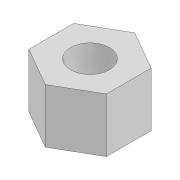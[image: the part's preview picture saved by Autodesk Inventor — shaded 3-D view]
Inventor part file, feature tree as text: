
AUTODESK INVENTOR PART (.ipt)
format: ipt  version: 2022 (Build 260153000, 153)  size: 83,968 bytes
history: native  units: mm
features: extrude x1, sketch x1
ambient origin geometry x8: Origin, YZ Plane, XZ Plane, XY Plane, X Axis, Y Axis, Z Axis, Center Point
bodies: Solid1 (feature_tree)
feature tree (2):
  extrude  "Extrusion1"  Depth=2.8mm
  sketch  "Sketch1"  dims[d0=4.0mm d1=2.0mm d2=2.8mm d3=0.0mm]
